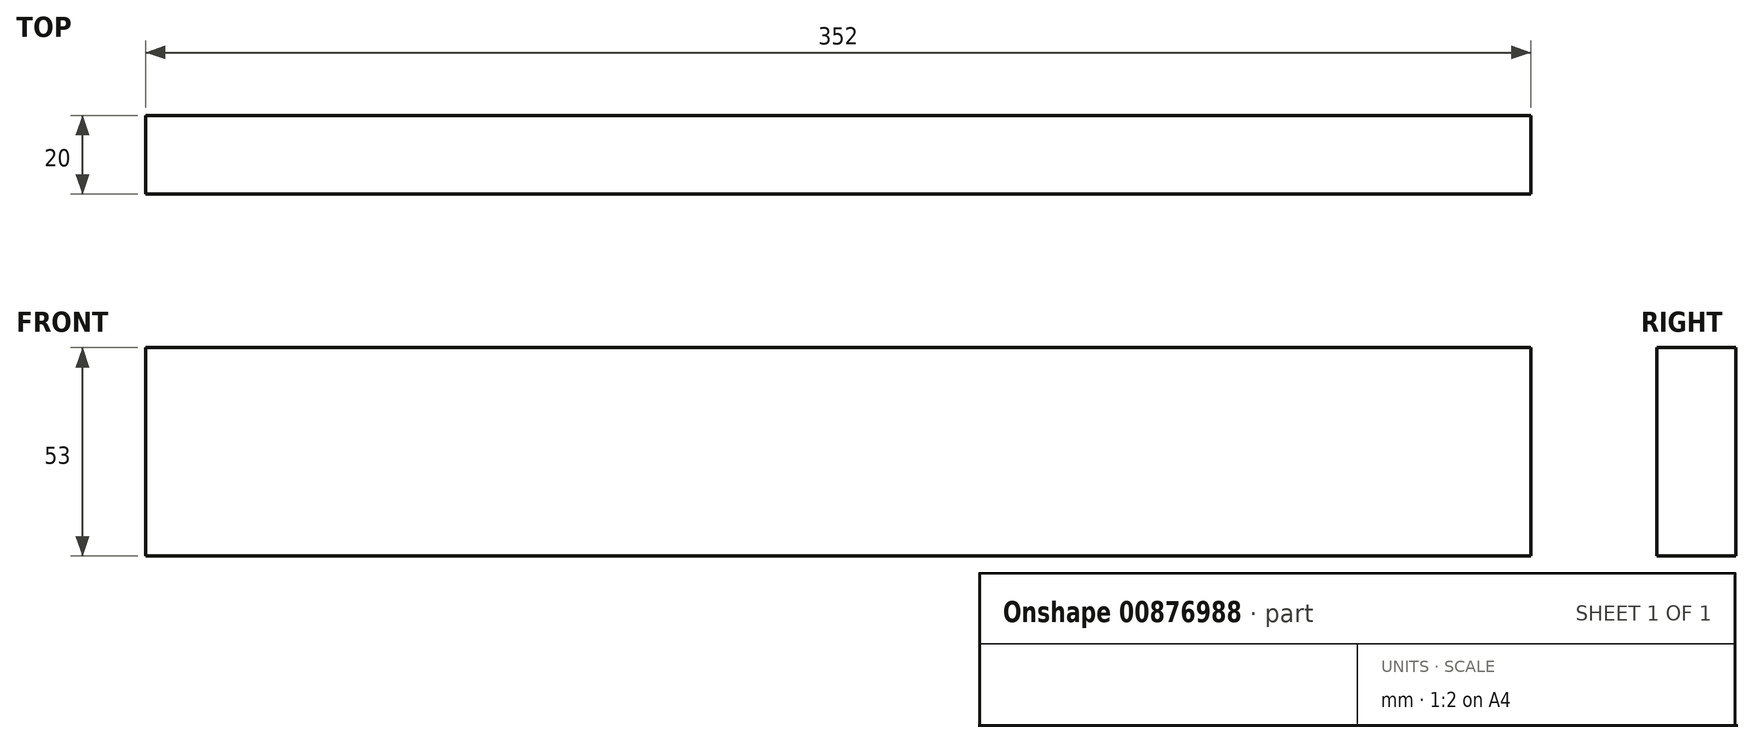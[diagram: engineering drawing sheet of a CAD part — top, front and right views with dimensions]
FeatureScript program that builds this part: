
annotation { "Feature Type Name" : "Feature", "Feature Type Description" : "" }
export const myFeature = defineFeature(function(context is Context, id is Id, definition is map)
    precondition{}
    {
        {
            var Q0;
            Q0=qCreatedBy(makeId("Front.planeOp"),FACE);
            var sketch = newSketch(context, id + "F0", { "sketchPlane" : qUnion([Q0])});
            skLineSegment(sketch, "E0.bottom", {"start": v(-176, 26.5) * mm, "end": v(176, 26.5) * mm});
            skLineSegment(sketch, "E0.top", {"start": v(-176, -26.5) * mm, "end": v(176, -26.5) * mm});
            skLineSegment(sketch, "E0.left", {"start": v(-176, 26.5) * mm, "end": v(-176, -26.5) * mm});
            skLineSegment(sketch, "E0.right", {"start": v(176, 26.5) * mm, "end": v(176, -26.5) * mm});
            skPoint(sketch, "E0.middle", {"position": v(0, 0) * mm});
            skSolve(sketch);
        }
        {
            var Q0;
            Q0=qSketchRegion(id+"F0",true);
            extrude(context, id + "F1", {"entities" : qUnion([Q0]), "flatOperationType" : FlatOperationType.REMOVE, "depth" : 20 * mm, "offsetDistance" : 25 * mm, "symmetric" : true, "domain" : OperationDomain.MODEL});
        }
    });
